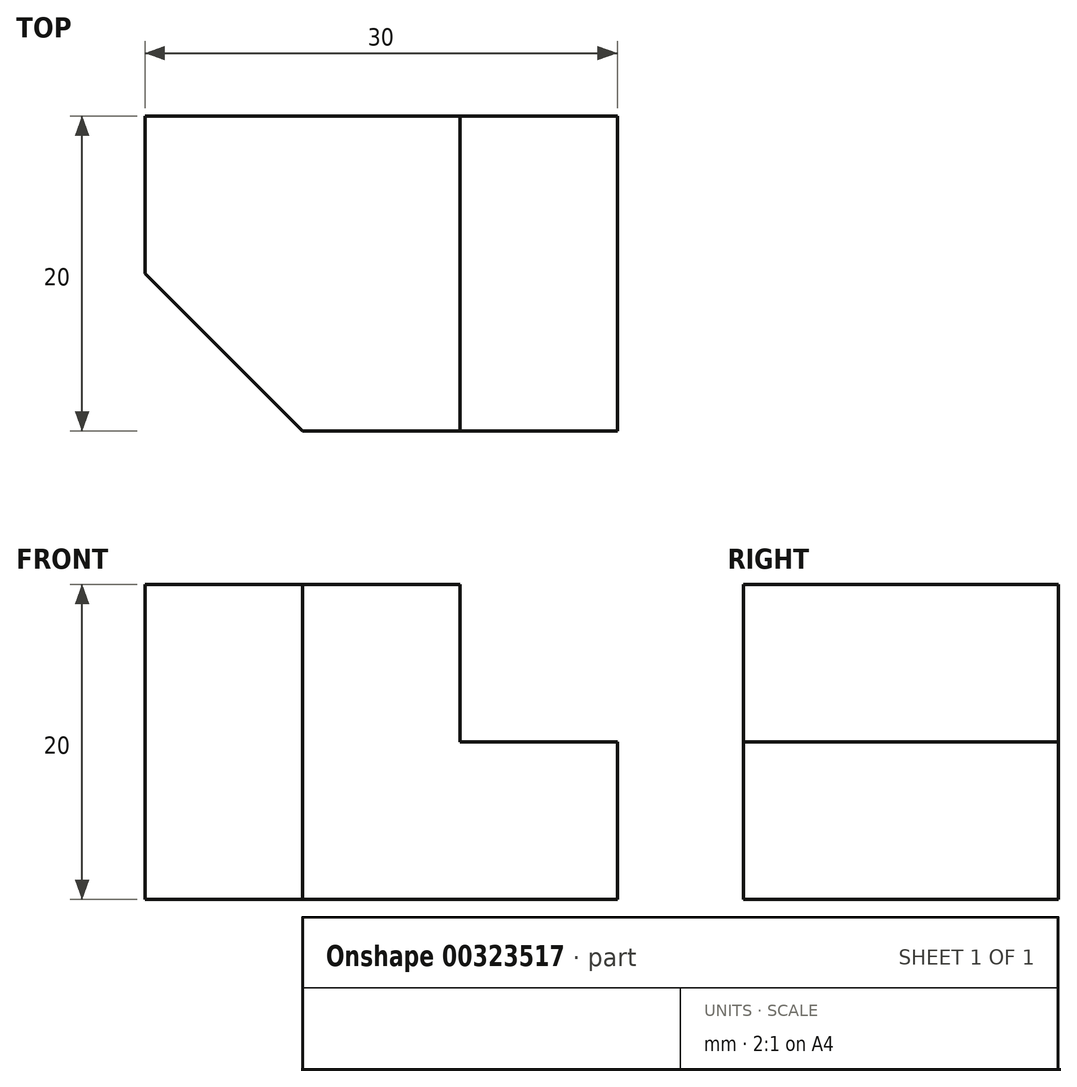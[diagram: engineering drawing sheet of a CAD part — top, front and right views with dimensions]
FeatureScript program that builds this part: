
annotation { "Feature Type Name" : "Feature", "Feature Type Description" : "" }
export const myFeature = defineFeature(function(context is Context, id is Id, definition is map)
    precondition{}
    {
        {
            var Q0;
            Q0=qCreatedBy(makeId("Front.planeOp"),FACE);
            var sketch = newSketch(context, id + "F0", { "sketchPlane" : qUnion([Q0])});
            skLineSegment(sketch, "E0", {"start": v(0, 0) * mm, "end": v(0, 20) * mm});
            skLineSegment(sketch, "E1", {"start": v(0, 20) * mm, "end": v(20, 20) * mm});
            skLineSegment(sketch, "E2", {"start": v(20, 20) * mm, "end": v(20, 10) * mm});
            skLineSegment(sketch, "E3", {"start": v(20, 10) * mm, "end": v(30, 10) * mm});
            skLineSegment(sketch, "E4", {"start": v(30, 10) * mm, "end": v(30, 0) * mm});
            skLineSegment(sketch, "E5", {"start": v(30, 0) * mm, "end": v(0, 0) * mm});
            skLineSegment(sketch, "E6", {"start": v(10, 20) * mm, "end": v(10, 0) * mm});
            skSolve(sketch);
        }
        {
            var Q0;
            {var subQ1=sQuery(id+"F0.wireOp",EDGE,"E2");Q0=makeQuery(id+"F0.imprint","IMPRINT",FACE,{"disambiguationData":[TD([[makeQuery(id+"F0.imprint","IMPRINT",EDGE,{"derivedFrom":subQ1}),-1.0]])]});}
            var Q1;
            {var subQ0=sQuery(id+"F0.wireOp",EDGE,"E0");Q1=makeQuery(id+"F0.imprint","IMPRINT",FACE,{"disambiguationData":[TD([[makeQuery(id+"F0.imprint","IMPRINT",EDGE,{"derivedFrom":subQ0}),-1.0]])]});}
            extrude(context, id + "F1", {"entities" : qUnion([Q0, Q1]), "oppositeDirection" : true, "depth" : 20 * mm, "symmetric" : true});
        }
        {
            var Q0;
            Q0=makeQuery(id+"F1.opExtrude","SWEPT_FACE",FACE,{"disambiguationData":[OSD([sQuery(id+"F0.wireOp",EDGE,"E1")])]});
            var sketch = newSketch(context, id + "F2", { "sketchPlane" : qUnion([Q0])});
            skLineSegment(sketch, "E7", {"start": v(0, 0) * mm, "end": v(0, -10) * mm});
            skLineSegment(sketch, "E8", {"start": v(0, -10) * mm, "end": v(10, -10) * mm});
            skLineSegment(sketch, "E9", {"start": v(10, -10) * mm, "end": v(0, 0) * mm});
            skSolve(sketch);
        }
        {
            var Q0;
            Q0=makeQuery(id+"F2.imprint","IMPRINT",FACE,{"disambiguationData":[TD([[makeQuery(id+"F2.imprint","IMPRINT",EDGE,{"derivedFrom":sQuery(id+"F2.wireOp",EDGE,"E7")}),1.0]])]});
            extrude(context, id + "F3", {"entities" : qUnion([Q0]), "operationType" : NewBodyOperationType.REMOVE, "endBound" : BoundingType.THROUGH_ALL, "oppositeDirection" : true, "depth" : 25 * mm});
        }
    });
